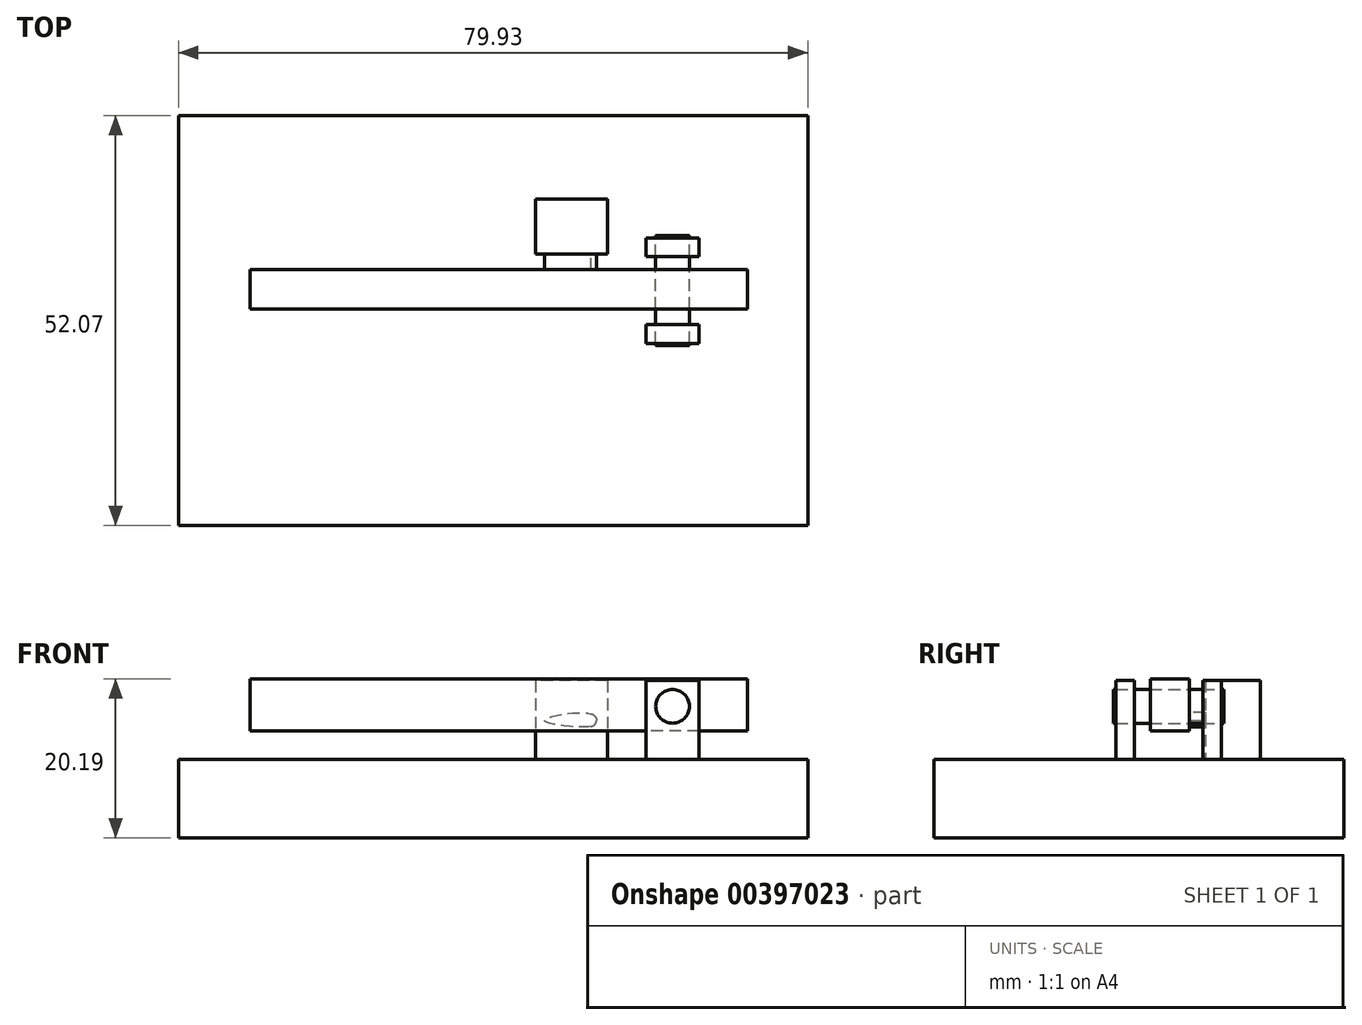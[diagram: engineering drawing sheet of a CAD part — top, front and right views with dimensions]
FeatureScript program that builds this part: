
annotation { "Feature Type Name" : "Feature", "Feature Type Description" : "" }
export const myFeature = defineFeature(function(context is Context, id is Id, definition is map)
    precondition{}
    {
        {
            var Q0;
            Q0=qCreatedBy(makeId("Top.planeOp"),FACE);
            var sketch = newSketch(context, id + "F0", { "sketchPlane" : qUnion([Q0])});
            skLineSegment(sketch, "E0.bottom", {"start": v(-34.2, 22.24) * mm, "end": v(45.74, 22.24) * mm});
            skLineSegment(sketch, "E0.top", {"start": v(-34.2, -29.83) * mm, "end": v(45.74, -29.83) * mm});
            skLineSegment(sketch, "E0.left", {"start": v(-34.2, 22.24) * mm, "end": v(-34.2, -29.83) * mm});
            skLineSegment(sketch, "E0.right", {"start": v(45.74, 22.24) * mm, "end": v(45.74, -29.83) * mm});
            skSolve(sketch);
        }
        {
            var Q0;
            Q0 = qSketchRegion(id + "F0", true);
            extrude(context, id + "F1", {"entities" : qUnion([Q0]), "oppositeDirection" : true, "depth" : 10 * mm});
        }
        {
            var Q0;
            Q0=makeQuery(id+"F1.opExtrude","CAP_FACE",FACE,{"disambiguationData":[OSD([sQuery(id+"F0.wireOp",EDGE,"E0.bottom"),sQuery(id+"F0.wireOp",EDGE,"E0.top"),sQuery(id+"F0.wireOp",EDGE,"E0.left"),sQuery(id+"F0.wireOp",EDGE,"E0.right")])],"isStart":true});
            var sketch = newSketch(context, id + "F2", { "sketchPlane" : qUnion([Q0])});
            skLineSegment(sketch, "E1.bottom", {"start": v(25.17, 6.7) * mm, "end": v(31.95, 6.7) * mm});
            skLineSegment(sketch, "E1.top", {"start": v(25.17, 4.33) * mm, "end": v(31.95, 4.33) * mm});
            skLineSegment(sketch, "E1.left", {"start": v(25.17, 6.7) * mm, "end": v(25.17, 4.33) * mm});
            skLineSegment(sketch, "E1.right", {"start": v(31.95, 6.7) * mm, "end": v(31.95, 4.33) * mm});
            skLineSegment(sketch, "E2", {"start": v(-34.2, 0) * mm, "end": v(45.74, 0) * mm, "construction": true});
            skLineSegment(sketch, "E3.MirrorCS", {"start": v(31.95, -6.7) * mm, "end": v(31.95, -4.33) * mm});
            skLineSegment(sketch, "E4.MirrorCS", {"start": v(25.17, -6.7) * mm, "end": v(25.17, -4.33) * mm});
            skLineSegment(sketch, "E5.MirrorCS", {"start": v(25.17, -4.33) * mm, "end": v(31.95, -4.33) * mm});
            skLineSegment(sketch, "E6.MirrorCS", {"start": v(25.17, -6.7) * mm, "end": v(31.95, -6.7) * mm});
            skSolve(sketch);
        }
        {
            var Q0;
            Q0 = qSketchRegion(id + "F2", true);
            extrude(context, id + "F3", {"entities" : qUnion([Q0]), "depth" : 10 * mm});
        }
        {
            var Q0;
            Q0=makeQuery(id+"F3.opExtrude","SWEPT_FACE",FACE,{"disambiguationData":[OSD([sQuery(id+"F2.wireOp",EDGE,"E6.MirrorCS")])]});
            var sketch = newSketch(context, id + "F4", { "sketchPlane" : qUnion([Q0])});
            skPoint(sketch, "E7", {"position": v(28.54, 7.05) * mm});
            skSolve(sketch);
        }
        {
            var Q0;
            Q0=sQuery(id+"F4.wireOp",VERTEX,"E7");
            var Q1;
            Q1=makeQuery(id+"F1.opExtrude","SWEPT_BODY",BODY,{"disambiguationData":[OSD([sQuery(id+"F0.wireOp",EDGE,"E0.bottom"),sQuery(id+"F0.wireOp",EDGE,"E0.top"),sQuery(id+"F0.wireOp",EDGE,"E0.left"),sQuery(id+"F0.wireOp",EDGE,"E0.right")])]});
            hole(context, id + "F5", {"style" : HoleStyle.SIMPLE, "endStyle" : HoleEndStyle.THROUGH, "holeDiameter" : 4 * mm, "isTappedThrough" : true, "tappedDepth" : 12 * mm, "tapClearance" : 3, "locations" : qUnion([Q0]), "scope" : qUnion([Q1])});
        }
        {
            var Q0;
            Q0=qCreatedBy(makeId("Front.planeOp"),FACE);
            var sketch = newSketch(context, id + "F6", { "sketchPlane" : qUnion([Q0])});
            skCircle(sketch, "E8", {"center": v(28.56, 6.71) * mm, "radius": 2.14 * mm});
            skSolve(sketch);
        }
        {
            var Q0;
            Q0=makeQuery(id+"F6.imprint","IMPRINT",FACE,{"disambiguationData":[TD([[makeQuery(id+"F6.imprint","IMPRINT",EDGE,{"derivedFrom":sQuery(id+"F6.wireOp",EDGE,"E8")}),1.0]])]});
            extrude(context, id + "F7", {"entities" : qUnion([Q0]), "endBound" : BoundingType.SYMMETRIC, "depth" : 14 * mm});
        }
        {
            var Q0;
            Q0=makeQuery(id+"F3.opExtrude","SWEPT_FACE",FACE,{"disambiguationData":[OSD([sQuery(id+"F2.wireOp",EDGE,"E5.MirrorCS")])]});
            cPlane(context, id + "F8", {"entities" : qUnion([Q0]), "cplaneType" : CPlaneType.OFFSET, "offset" : 4.5 * mm, "width" : 150 * mm, "height" : 150 * mm});
        }
        {
            var Q0;
            Q0=qCreatedBy(id+"F8.planeOp",FACE);
            var sketch = newSketch(context, id + "F9", { "sketchPlane" : qUnion([Q0])});
            skLineSegment(sketch, "E9.bottom", {"start": v(-38.06, 10.2) * mm, "end": v(25.12, 10.2) * mm});
            skLineSegment(sketch, "E9.top", {"start": v(-38.06, 3.6) * mm, "end": v(25.12, 3.6) * mm});
            skLineSegment(sketch, "E9.left", {"start": v(-38.06, 10.2) * mm, "end": v(-38.06, 3.6) * mm});
            skLineSegment(sketch, "E9.right", {"start": v(25.12, 10.2) * mm, "end": v(25.12, 3.6) * mm});
            skSolve(sketch);
        }
        {
            var Q0;
            Q0=makeQuery(id+"F9.imprint","IMPRINT",FACE,{"disambiguationData":[TD([[makeQuery(id+"F9.imprint","IMPRINT",EDGE,{"derivedFrom":sQuery(id+"F9.wireOp",EDGE,"E9.bottom")}),-1.0]])]});
            extrude(context, id + "F10", {"entities" : qUnion([Q0]), "endBound" : BoundingType.SYMMETRIC, "depth" : 5 * mm});
        }
        {
            var Q0;
            Q0=makeQuery(id+"F1.opExtrude","CAP_FACE",FACE,{"disambiguationData":[OSD([sQuery(id+"F0.wireOp",EDGE,"E0.bottom"),sQuery(id+"F0.wireOp",EDGE,"E0.top"),sQuery(id+"F0.wireOp",EDGE,"E0.left"),sQuery(id+"F0.wireOp",EDGE,"E0.right")])],"isStart":true});
            var sketch = newSketch(context, id + "F11", { "sketchPlane" : qUnion([Q0])});
            skLineSegment(sketch, "E10.bottom", {"start": v(20.28, 4.67) * mm, "end": v(11.17, 4.67) * mm});
            skLineSegment(sketch, "E10.top", {"start": v(20.28, 11.64) * mm, "end": v(11.17, 11.64) * mm});
            skLineSegment(sketch, "E10.left", {"start": v(20.28, 4.67) * mm, "end": v(20.28, 11.64) * mm});
            skLineSegment(sketch, "E10.right", {"start": v(11.17, 4.67) * mm, "end": v(11.17, 11.64) * mm});
            skSolve(sketch);
        }
        {
            var Q0;
            Q0=makeQuery(id+"F11.imprint","IMPRINT",FACE,{"disambiguationData":[TD([[makeQuery(id+"F11.imprint","IMPRINT",EDGE,{"derivedFrom":sQuery(id+"F11.wireOp",EDGE,"E10.bottom")}),-1.0]])]});
            extrude(context, id + "F12", {"entities" : qUnion([Q0]), "depth" : 10 * mm});
        }
        {
            var Q0;
            Q0=makeQuery(id+"F12.opExtrude","SWEPT_FACE",FACE,{"disambiguationData":[OSD([sQuery(id+"F11.wireOp",EDGE,"E10.bottom")])]});
            var sketch = newSketch(context, id + "F13", { "sketchPlane" : qUnion([Q0])});
            skArc(sketch, "E11", {"start": v(18.2, 4.14) * mm, "mid": v(18.9, 4.97) * mm, "end": v(18.17, 5.78) * mm});
            skPoint(sketch, "E12", {"position": v(12.3, 4.86) * mm});
            skPoint(sketch, "E13.3.internal.snap0", {"position": v(18.9, 4.97) * mm});
            skFitSpline(sketch, "E13", {"points": [v(18.2, 4.14) * mm, v(12.3, 4.86) * mm, v(18.17, 5.78) * mm, v(18.9, 4.94) * mm], "startDerivative": vector(-6.66, -1.6) * mm, "endDerivative": vector(0.3, -3.57) * mm});
            skSolve(sketch);
        }
        {
            var Q0;
            {var subQ0=sQuery(id+"F13.wireOp",EDGE,"E13");var subQ1=sQuery(id+"F13.wireOp",EDGE,"E11");var subQ2=makeQuery(id+"F13.imprint","INTERSECT",VERTEX,{"disambiguationData":[OD(0.0)],"derivedFrom":[subQ1,subQ0]});Q0=makeQuery(id+"F13.imprint","IMPRINT",FACE,{"disambiguationData":[TD([[makeQuery(id+"F13.imprint","IMPRINT",EDGE,{"disambiguationData":[TD([[subQ2,-1.0]])],"derivedFrom":subQ1}),1.0]])]});}
            extrude(context, id + "F14", {"entities" : qUnion([Q0]), "depth" : 2 * mm});
        }
    });
